# Revit family: 94826005
name_source: partatom
category: Modelos genéricos
revit_build: Autodesk Revit 2016 (Build: 20150220_1215(x64)
units: mm (PartAtom-declared; Revit-internal decimal feet)

## family parameters
Com base no plano de trabalho = Não
Compartilhado = Não
Corte com vazios quando carregados = Não
Cota do conector redondo = Utilizar diâmetro
Pode hospedar o vergalhão = Não
Ponto de cálculo do ambiente = Não
Sempre na vertical = Sim
Tipo de parte = Normal

## types (1)
- Tramontina New Colorful 90 - 94826004
    Comentários de tipos = Ler Manual de Instalação
    Código de montagem = 94826/005
    Descrição = New colorful 90 - 94826/005
    Desenvolvedor = Factory Cursos & Desenvolvimento
    Fabricante = Tramontina
    Frequencia = 60  [stored 0.19685 ft]
    Nivel de Ruido = 62 db
    Numero de Velocidades = 3
    Potencia Elétrica (220 V) = 190 W
    Referencia = 94826/005
    Site do desenvolvedor = www.factorycursos.com.br
    Tensão = 220  [stored 0.721785 ft]
    Tipo de imagem = <Nenhum>
    URL = www.tramontina.com.br
    Vazão Maxima = 600 m3/h

note: [stored X ft] marks values corroborated as IEEE doubles in the binary element streams (Revit-internal decimal feet)
